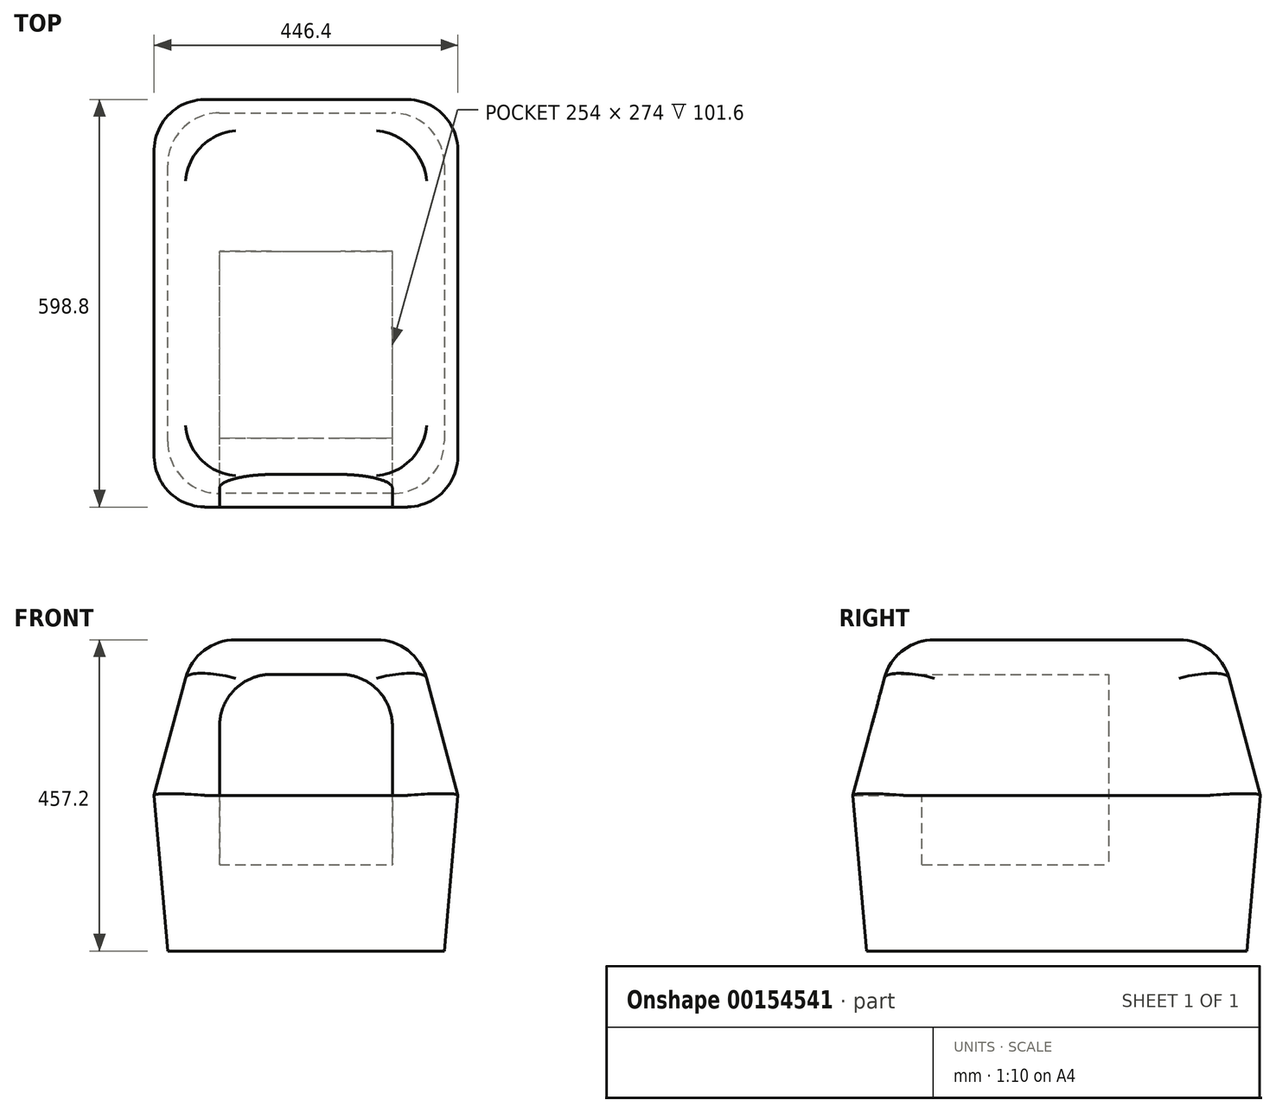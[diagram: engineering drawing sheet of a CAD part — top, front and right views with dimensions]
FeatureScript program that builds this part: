
annotation { "Feature Type Name" : "Feature", "Feature Type Description" : "" }
export const myFeature = defineFeature(function(context is Context, id is Id, definition is map)
    precondition{}
    {
        {
            var Q0;
            Q0=qCreatedBy(makeId("Top.planeOp"),FACE);
            var sketch = newSketch(context, id + "F0", { "sketchPlane" : qUnion([Q0])});
            skLineSegment(sketch, "E0.bottom", {"start": v(203.2, 279.4) * mm, "end": v(-203.2, 279.4) * mm});
            skLineSegment(sketch, "E0.top", {"start": v(203.2, -279.4) * mm, "end": v(-203.2, -279.4) * mm});
            skLineSegment(sketch, "E0.left", {"start": v(203.2, 279.4) * mm, "end": v(203.2, -279.4) * mm});
            skLineSegment(sketch, "E0.right", {"start": v(-203.2, 279.4) * mm, "end": v(-203.2, -279.4) * mm});
            skPoint(sketch, "E0.middle", {"position": v(0, 0) * mm});
            skSolve(sketch);
        }
        {
            var Q0;
            Q0=makeQuery(id+"F0.imprint","IMPRINT",FACE,{"disambiguationData":[TD([[makeQuery(id+"F0.imprint","IMPRINT",EDGE,{"derivedFrom":sQuery(id+"F0.wireOp",EDGE,"E0.bottom")}),1.0]])]});
            extrude(context, id + "F1", {"entities" : qUnion([Q0]), "depth" : 228.6 * mm, "hasDraft" : true, "draftAngle" : 5 * degree});
        }
        {
            var Q0;
            Q0=makeQuery(id+"F1.opExtrude","CAP_FACE",FACE,{"disambiguationData":[OSD([sQuery(id+"F0.wireOp",EDGE,"E0.bottom"),sQuery(id+"F0.wireOp",EDGE,"E0.top"),sQuery(id+"F0.wireOp",EDGE,"E0.left"),sQuery(id+"F0.wireOp",EDGE,"E0.right")])],"isStart":false});
            var sketch = newSketch(context, id + "F2", { "sketchPlane" : qUnion([Q0])});
            skLineSegment(sketch, "E1.bottom", {"start": v(-223.2, 299.4) * mm, "end": v(223.2, 299.4) * mm});
            skLineSegment(sketch, "E1.top", {"start": v(-223.2, -299.4) * mm, "end": v(223.2, -299.4) * mm});
            skLineSegment(sketch, "E1.left", {"start": v(-223.2, 299.4) * mm, "end": v(-223.2, -299.4) * mm});
            skLineSegment(sketch, "E1.right", {"start": v(223.2, 299.4) * mm, "end": v(223.2, -299.4) * mm});
            skSolve(sketch);
        }
        {
            var Q0;
            Q0=makeQuery(id+"F2.imprint","IMPRINT",FACE,{"disambiguationData":[TD([[makeQuery(id+"F2.imprint","IMPRINT",EDGE,{"derivedFrom":sQuery(id+"F2.wireOp",EDGE,"E1.bottom")}),1.0]])]});
            extrude(context, id + "F3", {"entities" : qUnion([Q0]), "operationType" : NewBodyOperationType.ADD, "depth" : 228.6 * mm, "hasDraft" : true, "draftAngle" : 15 * degree, "draftPullDirection" : true});
        }
        {
            var Q0;
            Q0=qCreatedBy(makeId("Front.planeOp"),FACE);
            var sketch = newSketch(context, id + "F4", { "sketchPlane" : qUnion([Q0])});
            skLineSegment(sketch, "E2.bottom", {"start": v(-127, 406.4) * mm, "end": v(127, 406.4) * mm});
            skLineSegment(sketch, "E2.top", {"start": v(-127, 228.6) * mm, "end": v(127, 228.6) * mm});
            skLineSegment(sketch, "E2.left", {"start": v(-127, 406.4) * mm, "end": v(-127, 228.6) * mm});
            skLineSegment(sketch, "E2.right", {"start": v(127, 406.4) * mm, "end": v(127, 228.6) * mm});
            skLineSegment(sketch, "E3", {"start": v(0, 0) * mm, "end": v(0, 228.6) * mm, "construction": true});
            skSolve(sketch);
        }
        {
            var Q0;
            Q0=makeQuery(id+"F4.imprint","IMPRINT",FACE,{"disambiguationData":[TD([[makeQuery(id+"F4.imprint","IMPRINT",EDGE,{"derivedFrom":sQuery(id+"F4.wireOp",EDGE,"E2.bottom")}),-1.0]])]});
            extrude(context, id + "F5", {"entities" : qUnion([Q0]), "operationType" : NewBodyOperationType.REMOVE, "endBound" : BoundingType.THROUGH_ALL, "depth" : 30.48 * mm, "hasSecondDirection" : true, "secondDirectionOppositeDirection" : true, "secondDirectionDepth" : 76.2 * mm});
        }
        {
            var Q0;
            Q0=makeQuery(id+"F5.boolean.opBoolean","COPY",EDGE,{"derivedFrom":makeQuery(id+"F5.opExtrude","SWEPT_EDGE",EDGE,{"disambiguationData":[OSD([sQuery(id+"F4.wireOp",EDGE,"E2.bottom"),sQuery(id+"F4.wireOp",EDGE,"E2.right")])]})});
            var Q1;
            Q1=makeQuery(id+"F5.boolean.opBoolean","COPY",EDGE,{"derivedFrom":makeQuery(id+"F5.opExtrude","SWEPT_EDGE",EDGE,{"disambiguationData":[OSD([sQuery(id+"F4.wireOp",EDGE,"E2.bottom"),sQuery(id+"F4.wireOp",EDGE,"E2.left")])]})});
            fillet(context, id + "F6", {"entities" : qUnion([Q0, Q1]), "radius" : 76.2 * mm, "tangentPropagation" : true, "allowEdgeOverflow" : false});
        }
        {
            var Q0;
            Q0=makeQuery(id+"F3.opExtrude","CAP_FACE",FACE,{"disambiguationData":[OSD([sQuery(id+"F2.wireOp",EDGE,"E1.bottom"),sQuery(id+"F2.wireOp",EDGE,"E1.top"),sQuery(id+"F2.wireOp",EDGE,"E1.left"),sQuery(id+"F2.wireOp",EDGE,"E1.right")])],"isStart":false});
            var Q1;
            Q1=makeQuery(id+"F3.opExtrude","SWEPT_EDGE",EDGE,{"disambiguationData":[OSD([sQuery(id+"F2.wireOp",EDGE,"E1.top"),sQuery(id+"F2.wireOp",EDGE,"E1.right")])]});
            var Q2;
            Q2=makeQuery(id+"F3.opExtrude","SWEPT_EDGE",EDGE,{"disambiguationData":[OSD([sQuery(id+"F2.wireOp",EDGE,"E1.top"),sQuery(id+"F2.wireOp",EDGE,"E1.left")])]});
            var Q3;
            Q3=makeQuery(id+"F1.opExtrude","SWEPT_EDGE",EDGE,{"disambiguationData":[OSD([sQuery(id+"F0.wireOp",EDGE,"E0.top"),sQuery(id+"F0.wireOp",EDGE,"E0.right")])]});
            var Q4;
            Q4=makeQuery(id+"F1.opExtrude","SWEPT_EDGE",EDGE,{"disambiguationData":[OSD([sQuery(id+"F0.wireOp",EDGE,"E0.top"),sQuery(id+"F0.wireOp",EDGE,"E0.left")])]});
            var Q5;
            Q5=makeQuery(id+"F3.opExtrude","SWEPT_EDGE",EDGE,{"disambiguationData":[OSD([sQuery(id+"F2.wireOp",EDGE,"E1.bottom"),sQuery(id+"F2.wireOp",EDGE,"E1.right")])]});
            var Q6;
            Q6=makeQuery(id+"F1.opExtrude","SWEPT_EDGE",EDGE,{"disambiguationData":[OSD([sQuery(id+"F0.wireOp",EDGE,"E0.bottom"),sQuery(id+"F0.wireOp",EDGE,"E0.left")])]});
            var Q7;
            Q7=makeQuery(id+"F3.opExtrude","SWEPT_EDGE",EDGE,{"disambiguationData":[OSD([sQuery(id+"F2.wireOp",EDGE,"E1.bottom"),sQuery(id+"F2.wireOp",EDGE,"E1.left")])]});
            var Q8;
            Q8=makeQuery(id+"F1.opExtrude","SWEPT_EDGE",EDGE,{"disambiguationData":[OSD([sQuery(id+"F0.wireOp",EDGE,"E0.bottom"),sQuery(id+"F0.wireOp",EDGE,"E0.right")])]});
            fillet(context, id + "F7", {"entities" : qUnion([Q0, Q1, Q2, Q3, Q4, Q5, Q6, Q7, Q8]), "radius" : 76.2 * mm, "tangentPropagation" : true, "allowEdgeOverflow" : false});
        }
        {
            var Q0;
            Q0=makeQuery(id+"F5.boolean.opBoolean","COPY",FACE,{"derivedFrom":makeQuery(id+"F5.opExtrude","SWEPT_FACE",FACE,{"disambiguationData":[OSD([sQuery(id+"F4.wireOp",EDGE,"E2.top")])]})});
            var sketch = newSketch(context, id + "F8", { "sketchPlane" : qUnion([Q0])});
            skLineSegment(sketch, "E4.bottom", {"start": v(-127, 76.2) * mm, "end": v(127, 76.2) * mm});
            skLineSegment(sketch, "E4.top", {"start": v(-127, -197.8) * mm, "end": v(127, -197.8) * mm});
            skLineSegment(sketch, "E4.left", {"start": v(-127, 76.2) * mm, "end": v(-127, -197.8) * mm});
            skLineSegment(sketch, "E4.right", {"start": v(127, 76.2) * mm, "end": v(127, -197.8) * mm});
            skSolve(sketch);
        }
        {
            var Q0;
            Q0=makeQuery(id+"F8.imprint","IMPRINT",FACE,{"disambiguationData":[TD([[makeQuery(id+"F8.imprint","IMPRINT",EDGE,{"derivedFrom":sQuery(id+"F8.wireOp",EDGE,"E4.bottom")}),-1.0]])]});
            extrude(context, id + "F9", {"entities" : qUnion([Q0]), "operationType" : NewBodyOperationType.REMOVE, "oppositeDirection" : true, "depth" : 101.6 * mm});
        }
    });
